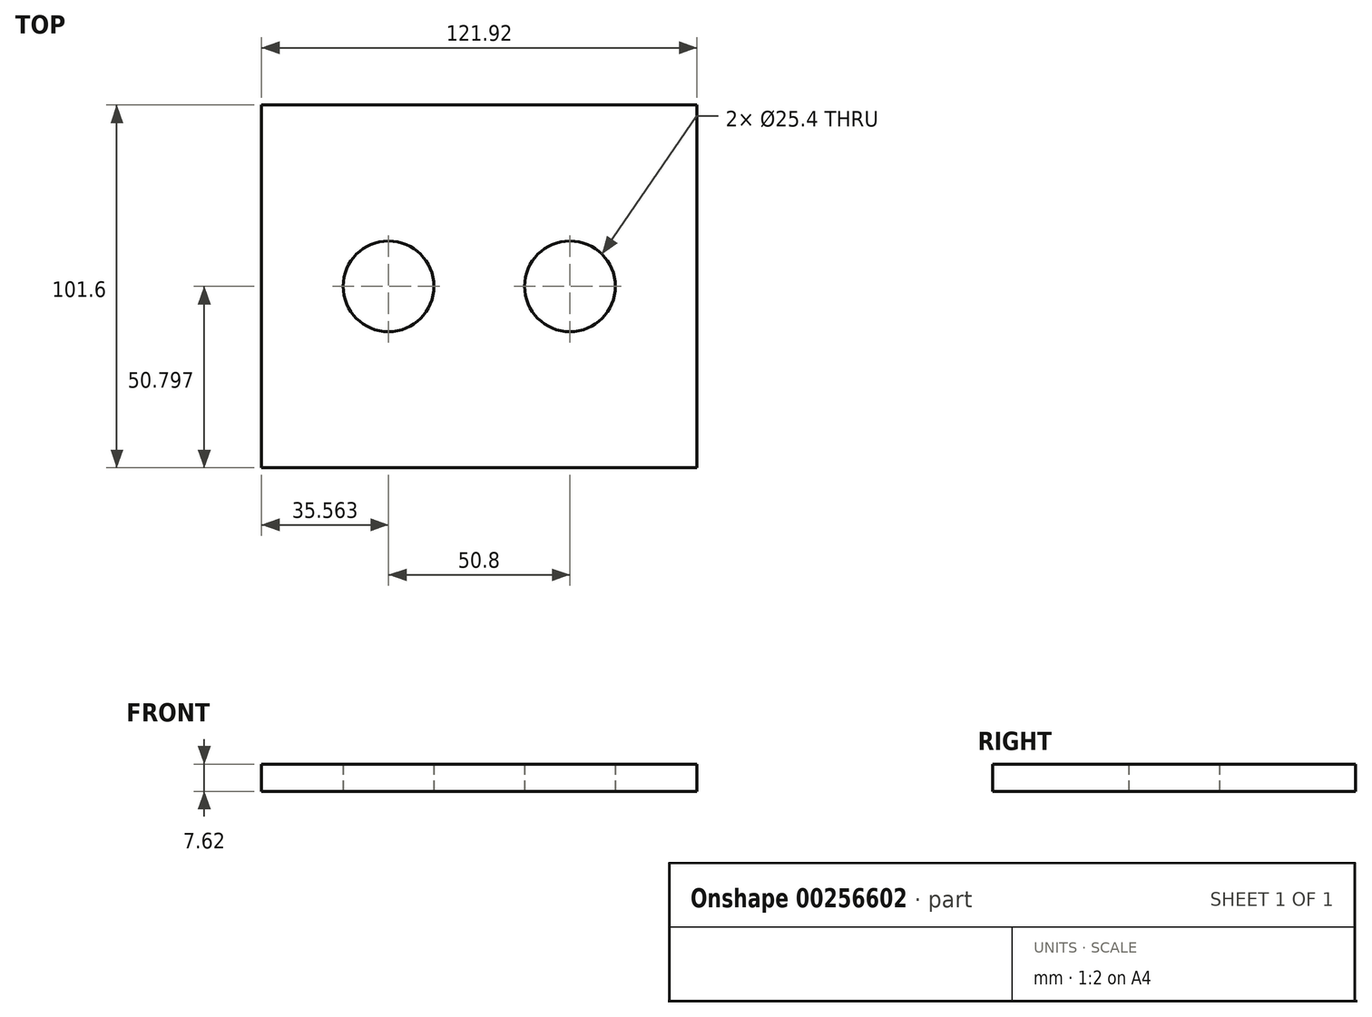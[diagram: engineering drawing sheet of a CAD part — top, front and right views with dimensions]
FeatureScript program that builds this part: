
annotation { "Feature Type Name" : "Feature", "Feature Type Description" : "" }
export const myFeature = defineFeature(function(context is Context, id is Id, definition is map)
    precondition{}
    {
        {
            var Q0;
            Q0=qCreatedBy(makeId("Top.planeOp"),FACE);
            var sketch = newSketch(context, id + "F0", { "sketchPlane" : qUnion([Q0])});
            skLineSegment(sketch, "E0.bottom", {"start": v(-63.12, 69.1) * mm, "end": v(58.8, 69.1) * mm});
            skLineSegment(sketch, "E0.top", {"start": v(-63.12, -32.5) * mm, "end": v(58.8, -32.5) * mm});
            skLineSegment(sketch, "E0.left", {"start": v(-63.12, 69.1) * mm, "end": v(-63.12, -32.5) * mm});
            skLineSegment(sketch, "E0.right", {"start": v(58.8, 69.1) * mm, "end": v(58.8, -32.5) * mm});
            skCircle(sketch, "E1", {"center": v(-27.56, 18.3) * mm, "radius": 12.7 * mm});
            skCircle(sketch, "E2", {"center": v(23.24, 18.3) * mm, "radius": 12.7 * mm});
            skSolve(sketch);
        }
        {
            var Q0;
            Q0=qSketchRegion(id+"F0",true);
            extrude(context, id + "F1", {"entities" : qUnion([Q0]), "depth" : 7.62 * mm});
        }
    });
